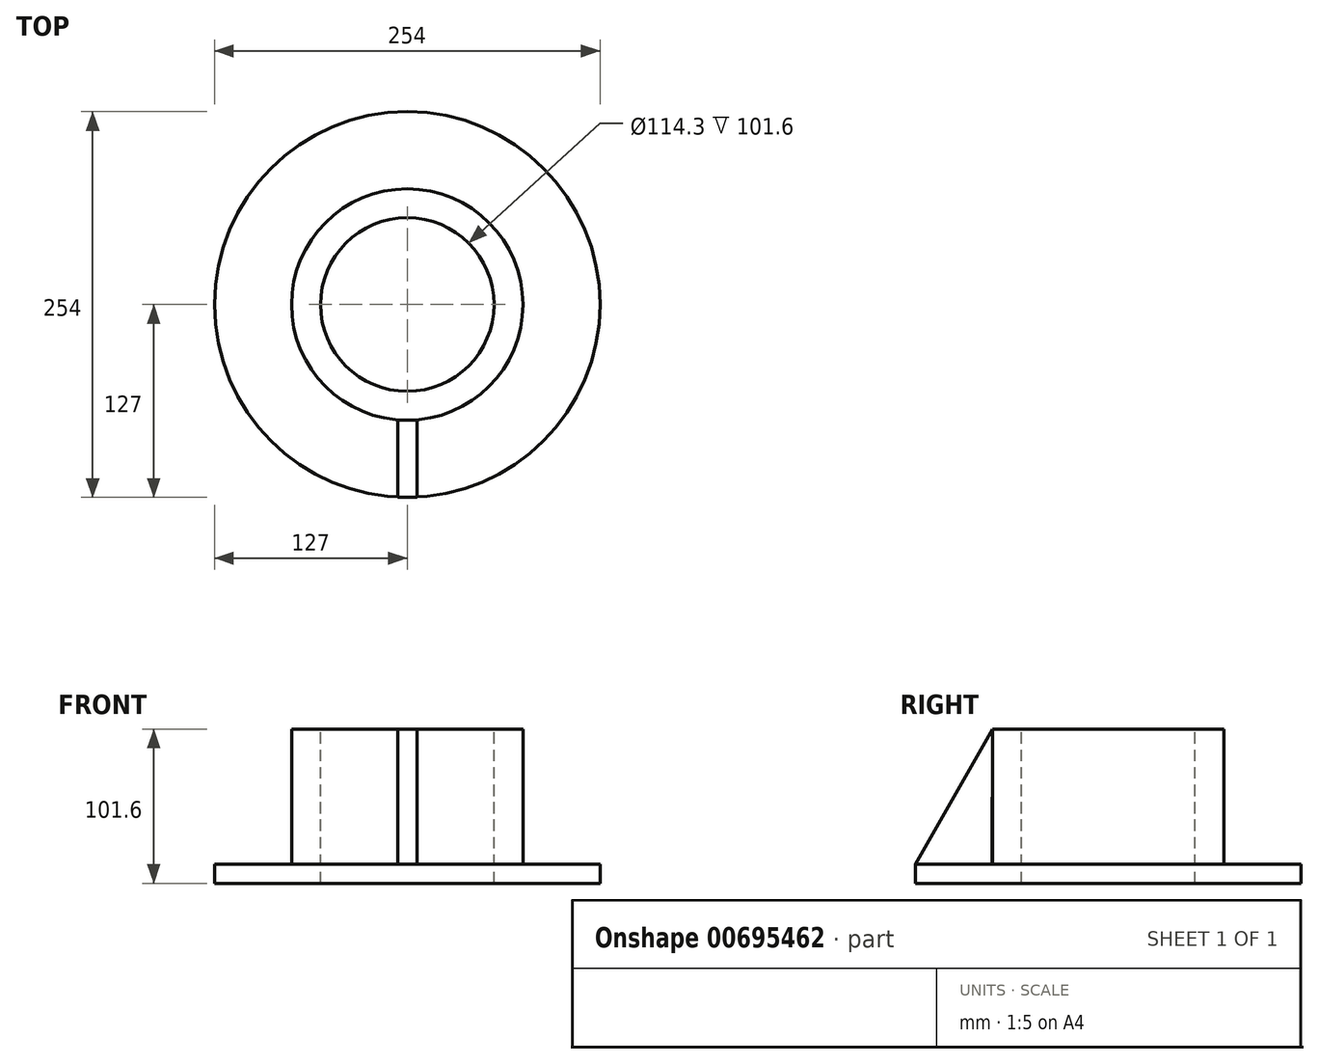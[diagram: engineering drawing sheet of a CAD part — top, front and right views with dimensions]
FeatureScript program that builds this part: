
annotation { "Feature Type Name" : "Feature", "Feature Type Description" : "" }
export const myFeature = defineFeature(function(context is Context, id is Id, definition is map)
    precondition{}
    {
        {
            var Q0;
            Q0=qCreatedBy(makeId("Front.planeOp"),FACE);
            var sketch = newSketch(context, id + "F0", { "sketchPlane" : qUnion([Q0])});
            skLineSegment(sketch, "E0.bottom", {"start": v(0, 0) * mm, "end": v(-127, 0) * mm});
            skLineSegment(sketch, "E0.top", {"start": v(0, 101.6) * mm, "end": v(-76.2, 101.6) * mm});
            skLineSegment(sketch, "E0.left", {"start": v(0, 0) * mm, "end": v(0, 101.6) * mm});
            skLineSegment(sketch, "E0.right", {"start": v(-127, 0) * mm, "end": v(-127, 12.7) * mm});
            skLineSegment(sketch, "E1", {"start": v(-127, 12.7) * mm, "end": v(-76.2, 12.7) * mm});
            skLineSegment(sketch, "E2", {"start": v(-76.2, 12.7) * mm, "end": v(-76.2, 101.6) * mm});
            skPoint(sketch, "E3.orphan", {"position": v(0, 12.7) * mm});
            skSolve(sketch);
        }
        {
            var Q0;
            Q0=qCreatedBy(makeId("Right.planeOp"),FACE);
            var sketch = newSketch(context, id + "F1", { "sketchPlane" : qUnion([Q0])});
            skLineSegment(sketch, "E4", {"start": v(0, -76.05) * mm, "end": v(0, 105.42) * mm, "construction": true});
            skSolve(sketch);
        }
        {
            var Q0;
            Q0=makeQuery(id+"F0.imprint","IMPRINT",FACE,{"disambiguationData":[TD([[makeQuery(id+"F0.imprint","IMPRINT",EDGE,{"derivedFrom":sQuery(id+"F0.wireOp",EDGE,"E0.bottom")}),-1.0]])]});
            var Q1;
            Q1=sQuery(id+"F1.wireOp",EDGE,"E4");
            revolve(context, id + "F2", {"surfaceOperationType" : NewSurfaceOperationType.NEW, "entities" : qUnion([Q0]), "axis" : qUnion([Q1]), "revolveType" : RevolveType.FULL});
        }
        {
            var Q0;
            Q0=makeQuery(id+"F2.opRevolve","SWEPT_FACE",FACE,{"disambiguationData":[OSD([sQuery(id+"F0.wireOp",EDGE,"E0.top")])]});
            var sketch = newSketch(context, id + "F3", { "sketchPlane" : qUnion([Q0])});
            skCircle(sketch, "E5", {"center": v(0, 0) * mm, "radius": 57.15 * mm});
            skSolve(sketch);
        }
        {
            var Q0;
            Q0=makeQuery(id+"F3.imprint","IMPRINT",FACE,{"disambiguationData":[TD([[makeQuery(id+"F3.imprint","IMPRINT",EDGE,{"derivedFrom":sQuery(id+"F3.wireOp",EDGE,"E5")}),1.0]])]});
            extrude(context, id + "F4", {"entities" : qUnion([Q0]), "operationType" : NewBodyOperationType.REMOVE, "endBound" : BoundingType.THROUGH_ALL, "oppositeDirection" : true, "depth" : 25.4 * mm, "offsetDistance" : 25.4 * mm});
        }
        {
            var Q0;
            Q0=qCreatedBy(makeId("Right.planeOp"),FACE);
            var sketch = newSketch(context, id + "F5", { "sketchPlane" : qUnion([Q0])});
            skLineSegment(sketch, "E6", {"start": v(-76.2, 101.6) * mm, "end": v(-127, 12.7) * mm});
            skLineSegment(sketch, "E7", {"start": v(-127, 12.7) * mm, "end": v(-76.37, 12.7) * mm});
            skLineSegment(sketch, "E8", {"start": v(-76.37, 12.7) * mm, "end": v(-76.2, 101.6) * mm});
            skSolve(sketch);
        }
        {
            var Q0;
            Q0 = qSketchRegion(id + "F5", true);
            extrude(context, id + "F6", {"entities" : qUnion([Q0]), "depth" : 12.7 * mm, "offsetDistance" : 25.4 * mm, "symmetric" : true});
        }
    });
